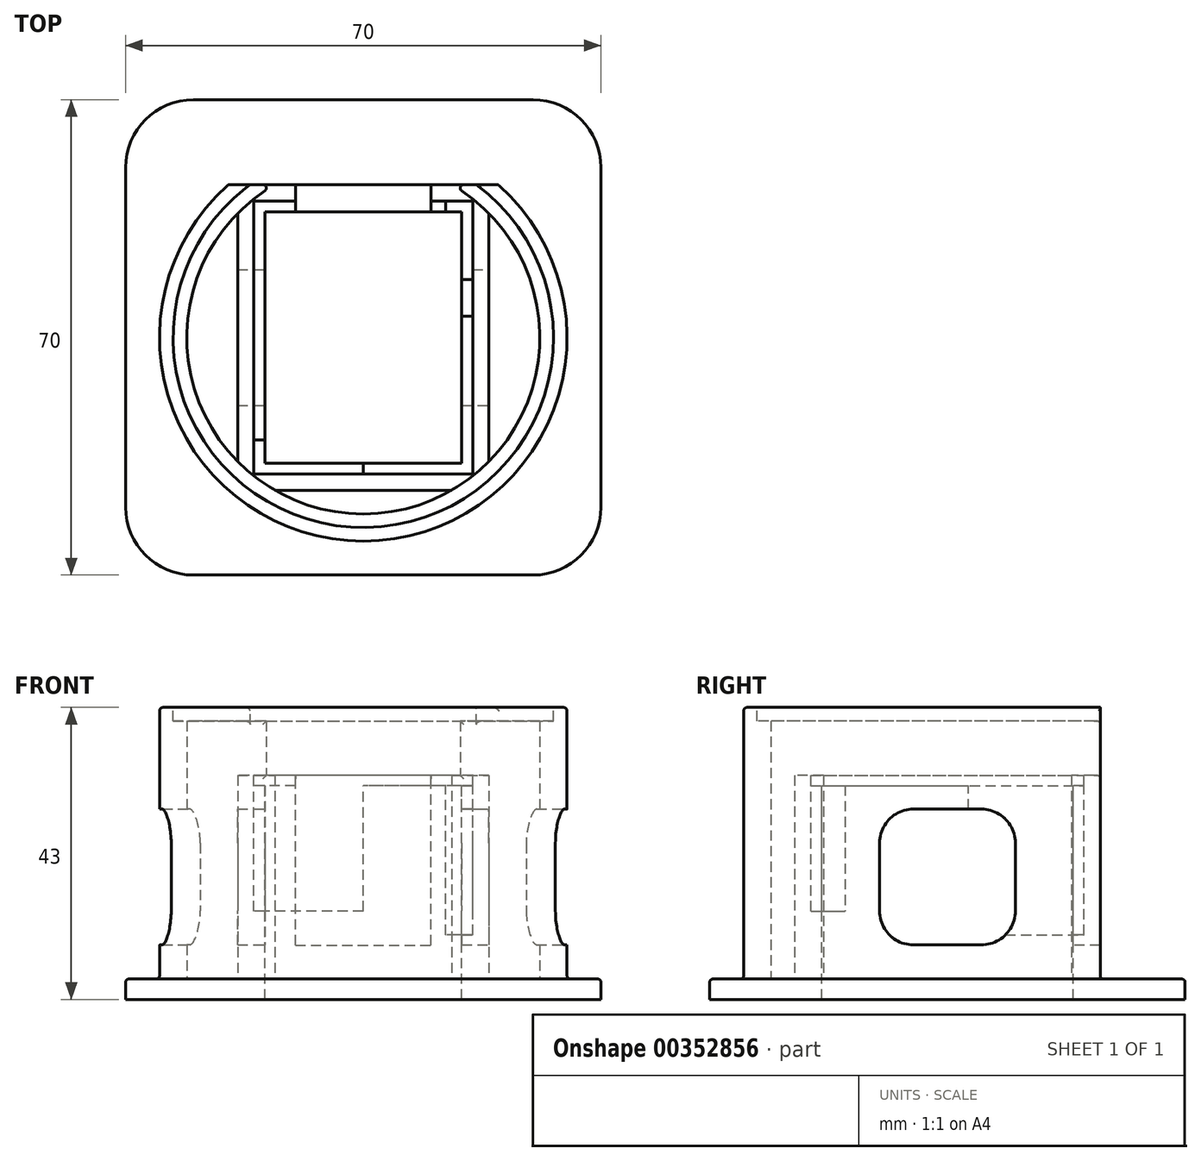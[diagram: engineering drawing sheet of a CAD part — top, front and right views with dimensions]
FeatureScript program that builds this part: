
annotation { "Feature Type Name" : "Feature", "Feature Type Description" : "" }
export const myFeature = defineFeature(function(context is Context, id is Id, definition is map)
    precondition{}
    {
        {
            var Q0;
            Q0=qCreatedBy(makeId("Top.planeOp"),FACE);
            var sketch = newSketch(context, id + "F0", { "sketchPlane" : qUnion([Q0])});
            skLineSegment(sketch, "E0.bottom", {"start": v(25, -35) * mm, "end": v(-25, -35) * mm});
            skLineSegment(sketch, "E0.top", {"start": v(25, 35) * mm, "end": v(-25, 35) * mm});
            skLineSegment(sketch, "E0.left", {"start": v(35, -25) * mm, "end": v(35, 25) * mm});
            skLineSegment(sketch, "E0.right", {"start": v(-35, -25) * mm, "end": v(-35, 25) * mm});
            skPoint(sketch, "E0.middle", {"position": v(0, 0) * mm});
            skPoint(sketch, "E1.visualSharp", {"position": v(-35, -35) * mm});
            skArc(sketch, "E1.filletArc", {"start": v(-35, -25) * mm, "mid": v(-32.07, -32.07) * mm, "end": v(-25, -35) * mm});
            skPoint(sketch, "E2.visualSharp", {"position": v(35, -35) * mm});
            skArc(sketch, "E2.filletArc", {"start": v(25, -35) * mm, "mid": v(32.07, -32.07) * mm, "end": v(35, -25) * mm});
            skPoint(sketch, "E3.visualSharp", {"position": v(35, 35) * mm});
            skArc(sketch, "E3.filletArc", {"start": v(35, 25) * mm, "mid": v(32.07, 32.07) * mm, "end": v(25, 35) * mm});
            skPoint(sketch, "E4.visualSharp", {"position": v(-35, 35) * mm});
            skArc(sketch, "E4.filletArc", {"start": v(-25, 35) * mm, "mid": v(-32.07, 32.07) * mm, "end": v(-35, 25) * mm});
            skSolve(sketch);
        }
        {
            var Q0;
            Q0 = qSketchRegion(id + "F0", true);
            extrude(context, id + "F1", {"entities" : qUnion([Q0]), "depth" : 3 * mm, "offsetDistance" : 25 * mm});
        }
        {
            var Q0;
            Q0=makeQuery(id+"F1.opExtrude","CAP_FACE",FACE,{"disambiguationData":[OSD([sQuery(id+"F0.wireOp",EDGE,"E0.bottom"),sQuery(id+"F0.wireOp",EDGE,"E0.top"),sQuery(id+"F0.wireOp",EDGE,"E0.left"),sQuery(id+"F0.wireOp",EDGE,"E0.right"),sQuery(id+"F0.wireOp",EDGE,"E1.filletArc"),sQuery(id+"F0.wireOp",EDGE,"E2.filletArc"),sQuery(id+"F0.wireOp",EDGE,"E3.filletArc"),sQuery(id+"F0.wireOp",EDGE,"E4.filletArc")])],"isStart":false});
            var sketch = newSketch(context, id + "F2", { "sketchPlane" : qUnion([Q0])});
            skLineSegment(sketch, "E5.bottom", {"start": v(16.5, -22.5) * mm, "end": v(-16.5, -22.5) * mm});
            skLineSegment(sketch, "E5.top", {"start": v(16.5, 22.5) * mm, "end": v(-16.5, 22.5) * mm});
            skLineSegment(sketch, "E5.left", {"start": v(18.5, -20.5) * mm, "end": v(18.5, 20.5) * mm});
            skLineSegment(sketch, "E5.right", {"start": v(-18.5, -20.5) * mm, "end": v(-18.5, 20.5) * mm});
            skPoint(sketch, "E5.middle", {"position": v(0, 0) * mm});
            skPoint(sketch, "E6.visualSharp", {"position": v(18.5, -22.5) * mm});
            skArc(sketch, "E6.filletArc", {"start": v(16.5, -22.5) * mm, "mid": v(17.91, -21.91) * mm, "end": v(18.5, -20.5) * mm});
            skPoint(sketch, "E7.visualSharp", {"position": v(18.5, 22.5) * mm});
            skArc(sketch, "E7.filletArc", {"start": v(18.5, 20.5) * mm, "mid": v(17.91, 21.91) * mm, "end": v(16.5, 22.5) * mm});
            skPoint(sketch, "E8.visualSharp", {"position": v(-18.5, 22.5) * mm});
            skArc(sketch, "E8.filletArc", {"start": v(-16.5, 22.5) * mm, "mid": v(-17.91, 21.91) * mm, "end": v(-18.5, 20.5) * mm});
            skPoint(sketch, "E9.visualSharp", {"position": v(-18.5, -22.5) * mm});
            skArc(sketch, "E9.filletArc", {"start": v(-18.5, -20.5) * mm, "mid": v(-17.91, -21.91) * mm, "end": v(-16.5, -22.5) * mm});
            skSolve(sketch);
        }
        {
            var Q0;
            Q0=makeQuery(id+"F2.imprint","IMPRINT",FACE,{"disambiguationData":[TD([[makeQuery(id+"F2.imprint","IMPRINT",EDGE,{"derivedFrom":sQuery(id+"F2.wireOp",EDGE,"E5.bottom")}),-1.0]])]});
            extrude(context, id + "F3", {"entities" : qUnion([Q0]), "operationType" : NewBodyOperationType.ADD, "depth" : 30 * mm, "offsetDistance" : 25 * mm});
        }
        {
            var Q0;
            Q0=makeQuery(id+"F3.opExtrude","CAP_FACE",FACE,{"disambiguationData":[OSD([sQuery(id+"F2.wireOp",EDGE,"E5.bottom"),sQuery(id+"F2.wireOp",EDGE,"E5.top"),sQuery(id+"F2.wireOp",EDGE,"E5.left"),sQuery(id+"F2.wireOp",EDGE,"E5.right"),sQuery(id+"F2.wireOp",EDGE,"E6.filletArc"),sQuery(id+"F2.wireOp",EDGE,"E7.filletArc"),sQuery(id+"F2.wireOp",EDGE,"E8.filletArc"),sQuery(id+"F2.wireOp",EDGE,"E9.filletArc")])],"isStart":false});
            var sketch = newSketch(context, id + "F4", { "sketchPlane" : qUnion([Q0])});
            skLineSegment(sketch, "E10.bottom", {"start": v(-14.5, 18.5) * mm, "end": v(14.5, 18.5) * mm});
            skLineSegment(sketch, "E10.top", {"start": v(-14.5, -18.5) * mm, "end": v(14.5, -18.5) * mm});
            skLineSegment(sketch, "E10.left", {"start": v(-14.5, 18.5) * mm, "end": v(-14.5, -18.5) * mm});
            skLineSegment(sketch, "E10.right", {"start": v(14.5, 18.5) * mm, "end": v(14.5, -18.5) * mm});
            skPoint(sketch, "E10.middle", {"position": v(0, 0) * mm});
            skSolve(sketch);
        }
        {
            var Q0;
            Q0=makeQuery(id+"F4.imprint","IMPRINT",FACE,{"disambiguationData":[TD([[makeQuery(id+"F4.imprint","IMPRINT",EDGE,{"derivedFrom":sQuery(id+"F4.wireOp",EDGE,"E10.bottom")}),-1.0]])]});
            extrude(context, id + "F5", {"entities" : qUnion([Q0]), "operationType" : NewBodyOperationType.REMOVE, "endBound" : BoundingType.THROUGH_ALL, "oppositeDirection" : true, "depth" : 25 * mm});
        }
        {
            var Q0;
            Q0=makeQuery(id+"F3.opExtrude","CAP_FACE",FACE,{"disambiguationData":[OSD([sQuery(id+"F2.wireOp",EDGE,"E5.bottom"),sQuery(id+"F2.wireOp",EDGE,"E5.top"),sQuery(id+"F2.wireOp",EDGE,"E5.left"),sQuery(id+"F2.wireOp",EDGE,"E5.right"),sQuery(id+"F2.wireOp",EDGE,"E6.filletArc"),sQuery(id+"F2.wireOp",EDGE,"E7.filletArc"),sQuery(id+"F2.wireOp",EDGE,"E8.filletArc"),sQuery(id+"F2.wireOp",EDGE,"E9.filletArc")])],"isStart":false});
            var sketch = newSketch(context, id + "F6", { "sketchPlane" : qUnion([Q0])});
            skLineSegment(sketch, "E11.bottom", {"start": v(16.1, -20.1) * mm, "end": v(-16.1, -20.1) * mm});
            skLineSegment(sketch, "E11.top", {"start": v(16.1, 20.1) * mm, "end": v(-16.1, 20.1) * mm});
            skLineSegment(sketch, "E11.left", {"start": v(16.1, -20.1) * mm, "end": v(16.1, 20.1) * mm});
            skLineSegment(sketch, "E11.right", {"start": v(-16.1, -20.1) * mm, "end": v(-16.1, 20.1) * mm});
            skPoint(sketch, "E11.middle", {"position": v(0, 0) * mm});
            skSolve(sketch);
        }
        {
            var Q0;
            Q0 = qSketchRegion(id + "F6", true);
            extrude(context, id + "F7", {"entities" : qUnion([Q0]), "operationType" : NewBodyOperationType.REMOVE, "oppositeDirection" : true, "depth" : 1.5 * mm});
        }
        {
            var Q0;
            Q0=makeQuery(id+"F7.boolean.opBoolean","COPY",FACE,{"derivedFrom":makeQuery(id+"F7.opExtrude","CAP_FACE",FACE,{"disambiguationData":[OSD([sQuery(id+"F6.wireOp",EDGE,"E11.bottom"),sQuery(id+"F6.wireOp",EDGE,"E11.top"),sQuery(id+"F6.wireOp",EDGE,"E11.left"),sQuery(id+"F6.wireOp",EDGE,"E11.right")])],"isStart":false})});
            var sketch = newSketch(context, id + "F8", { "sketchPlane" : qUnion([Q0])});
            skLineSegment(sketch, "E12.bottom", {"start": v(12.1, 20.1) * mm, "end": v(16.1, 20.1) * mm});
            skLineSegment(sketch, "E12.top", {"start": v(12.1, 3.1) * mm, "end": v(16.1, 3.1) * mm});
            skLineSegment(sketch, "E12.left", {"start": v(12.1, 20.1) * mm, "end": v(12.1, 3.1) * mm});
            skLineSegment(sketch, "E12.right", {"start": v(16.1, 20.1) * mm, "end": v(16.1, 3.1) * mm});
            skSolve(sketch);
        }
        {
            var Q0;
            {var subQ0=sQuery(id+"F8.wireOp",EDGE,"E12.right");var subQ1=sQuery(id+"F8.wireOp",EDGE,"E12.top");var subQ2=makeQuery(id+"F8.imprint","INTERSECT",VERTEX,{"derivedFrom":[subQ1,subQ0]});Q0=makeQuery(id+"F8.imprint","IMPRINT",FACE,{"disambiguationData":[TD([[makeQuery(id+"F8.imprint","IMPRINT",EDGE,{"disambiguationData":[TD([[subQ2,1.0]])],"derivedFrom":subQ1}),1.0]])]});}
            var Q1;
            {var subQ1=sQuery(id+"F8.wireOp",EDGE,"E12.bottom");Q1=makeQuery(id+"F8.imprint","IMPRINT",FACE,{"disambiguationData":[TD([[makeQuery(id+"F8.imprint","IMPRINT",EDGE,{"derivedFrom":subQ1}),1.0]])]});}
            extrude(context, id + "F9", {"entities" : qUnion([Q0, Q1]), "operationType" : NewBodyOperationType.REMOVE, "oppositeDirection" : true, "depth" : 22 * mm});
        }
        {
            var Q0;
            Q0=makeQuery(id+"F3.opExtrude","CAP_FACE",FACE,{"disambiguationData":[OSD([sQuery(id+"F2.wireOp",EDGE,"E5.bottom"),sQuery(id+"F2.wireOp",EDGE,"E5.top"),sQuery(id+"F2.wireOp",EDGE,"E5.left"),sQuery(id+"F2.wireOp",EDGE,"E5.right"),sQuery(id+"F2.wireOp",EDGE,"E6.filletArc"),sQuery(id+"F2.wireOp",EDGE,"E7.filletArc"),sQuery(id+"F2.wireOp",EDGE,"E8.filletArc"),sQuery(id+"F2.wireOp",EDGE,"E9.filletArc")])],"isStart":false});
            var sketch = newSketch(context, id + "F10", { "sketchPlane" : qUnion([Q0])});
            skLineSegment(sketch, "E13.bottom", {"start": v(-10, 22.5) * mm, "end": v(10, 22.5) * mm});
            skLineSegment(sketch, "E13.top", {"start": v(-10, 18.5) * mm, "end": v(10, 18.5) * mm});
            skLineSegment(sketch, "E13.left", {"start": v(-10, 22.5) * mm, "end": v(-10, 18.5) * mm});
            skLineSegment(sketch, "E13.right", {"start": v(10, 22.5) * mm, "end": v(10, 18.5) * mm});
            skSolve(sketch);
        }
        {
            var Q0;
            Q0 = qSketchRegion(id + "F10", true);
            extrude(context, id + "F11", {"entities" : qUnion([Q0]), "operationType" : NewBodyOperationType.REMOVE, "oppositeDirection" : true, "depth" : 25 * mm, "offsetDistance" : 25 * mm});
        }
        {
            var Q0;
            Q0=makeQuery(id+"F3.opExtrude","CAP_FACE",FACE,{"disambiguationData":[OSD([sQuery(id+"F2.wireOp",EDGE,"E5.bottom"),sQuery(id+"F2.wireOp",EDGE,"E5.top"),sQuery(id+"F2.wireOp",EDGE,"E5.left"),sQuery(id+"F2.wireOp",EDGE,"E5.right"),sQuery(id+"F2.wireOp",EDGE,"E6.filletArc"),sQuery(id+"F2.wireOp",EDGE,"E7.filletArc"),sQuery(id+"F2.wireOp",EDGE,"E8.filletArc"),sQuery(id+"F2.wireOp",EDGE,"E9.filletArc")])],"isStart":false});
            var sketch = newSketch(context, id + "F12", { "sketchPlane" : qUnion([Q0])});
            skLineSegment(sketch, "E14.bottom", {"start": v(0, -20.1) * mm, "end": v(-16.1, -20.1) * mm});
            skLineSegment(sketch, "E14.top", {"start": v(0, -15.1) * mm, "end": v(-16.1, -15.1) * mm});
            skLineSegment(sketch, "E14.left", {"start": v(0, -20.1) * mm, "end": v(0, -15.1) * mm});
            skLineSegment(sketch, "E14.right", {"start": v(-16.1, -20.1) * mm, "end": v(-16.1, -15.1) * mm});
            skSolve(sketch);
        }
        {
            var Q0;
            Q0 = qSketchRegion(id + "F12", true);
            extrude(context, id + "F13", {"entities" : qUnion([Q0]), "operationType" : NewBodyOperationType.REMOVE, "oppositeDirection" : true, "depth" : 20 * mm, "offsetDistance" : 25 * mm});
        }
        {
            var Q0;
            Q0=makeQuery(id+"F1.opExtrude","CAP_FACE",FACE,{"disambiguationData":[OSD([sQuery(id+"F0.wireOp",EDGE,"E0.bottom"),sQuery(id+"F0.wireOp",EDGE,"E0.top"),sQuery(id+"F0.wireOp",EDGE,"E0.left"),sQuery(id+"F0.wireOp",EDGE,"E0.right"),sQuery(id+"F0.wireOp",EDGE,"E1.filletArc"),sQuery(id+"F0.wireOp",EDGE,"E2.filletArc"),sQuery(id+"F0.wireOp",EDGE,"E3.filletArc"),sQuery(id+"F0.wireOp",EDGE,"E4.filletArc")])],"isStart":false});
            var sketch = newSketch(context, id + "F14", { "sketchPlane" : qUnion([Q0])});
            skArc(sketch, "E15", {"start": v(-19.84, 22.5) * mm, "mid": v(0, -30) * mm, "end": v(19.84, 22.5) * mm});
            skArc(sketch, "E16.0", {"start": v(-13.03, 22.5) * mm, "mid": v(0, -26) * mm, "end": v(13.03, 22.5) * mm});
            skLineSegment(sketch, "E17", {"start": v(13.03, 22.5) * mm, "end": v(19.84, 22.5) * mm});
            skLineSegment(sketch, "E18", {"start": v(19.84, 22.5) * mm, "end": v(13.03, 22.5) * mm});
            skLineSegment(sketch, "E19.trimOffspring", {"start": v(-13.03, 22.5) * mm, "end": v(-19.84, 22.5) * mm});
            skSolve(sketch);
        }
        {
            var Q0;
            Q0 = qSketchRegion(id + "F14", true);
            extrude(context, id + "F15", {"entities" : qUnion([Q0]), "operationType" : NewBodyOperationType.ADD, "depth" : 40 * mm, "offsetDistance" : 25 * mm});
        }
        {
            var Q0;
            Q0=makeQuery(id+"F15.opExtrude","CAP_FACE",FACE,{"disambiguationData":[OSD([sQuery(id+"F14.wireOp",EDGE,"E15"),sQuery(id+"F14.wireOp",EDGE,"E16.0"),sQuery(id+"F14.wireOp",EDGE,"E18"),sQuery(id+"F14.wireOp",EDGE,"E19.trimOffspring")])],"isStart":false});
            var sketch = newSketch(context, id + "F16", { "sketchPlane" : qUnion([Q0])});
            skCircle(sketch, "E20", {"center": v(0, 0) * mm, "radius": 28 * mm});
            skSolve(sketch);
        }
        {
            var Q0;
            Q0 = qSketchRegion(id + "F16", true);
            extrude(context, id + "F17", {"entities" : qUnion([Q0]), "operationType" : NewBodyOperationType.REMOVE, "oppositeDirection" : true, "depth" : 2 * mm, "offsetDistance" : 25 * mm});
        }
        {
            var Q0;
            Q0=makeQuery(id+"F7.boolean.opBoolean","COPY",EDGE,{"derivedFrom":makeQuery(id+"F7.opExtrude","CAP_EDGE",EDGE,{"disambiguationData":[OSD([sQuery(id+"F6.wireOp",EDGE,"E11.right")])],"isStart":true})});
            var Q1;
            {var subQ0=sQuery(id+"F6.wireOp",EDGE,"E11.top");Q1=makeQuery(id+"F11.boolean.opBoolean","SPLIT",EDGE,{"disambiguationData":[TD([makeQuery(id+"F7.boolean.opBoolean","COPY",FACE,{"derivedFrom":makeQuery(id+"F7.opExtrude","SWEPT_FACE",FACE,{"disambiguationData":[OSD([sQuery(id+"F6.wireOp",EDGE,"E11.left")])]})})])],"derivedFrom":makeQuery(id+"F7.boolean.opBoolean","COPY",EDGE,{"derivedFrom":makeQuery(id+"F7.opExtrude","CAP_EDGE",EDGE,{"disambiguationData":[OSD([subQ0])],"isStart":true})})});}
            var Q2;
            Q2=makeQuery(id+"F7.boolean.opBoolean","COPY",EDGE,{"derivedFrom":makeQuery(id+"F7.opExtrude","CAP_EDGE",EDGE,{"disambiguationData":[OSD([sQuery(id+"F6.wireOp",EDGE,"E11.left")])],"isStart":true})});
            var Q3;
            Q3=makeQuery(id+"F7.boolean.opBoolean","COPY",EDGE,{"derivedFrom":makeQuery(id+"F7.opExtrude","CAP_EDGE",EDGE,{"disambiguationData":[OSD([sQuery(id+"F6.wireOp",EDGE,"E11.bottom")])],"isStart":true})});
            var Q4;
            Q4=makeQuery(id+"F17.boolean.opBoolean","COPY",EDGE,{"derivedFrom":makeQuery(id+"F17.opExtrude","CAP_EDGE",EDGE,{"disambiguationData":[OSD([sQuery(id+"F16.wireOp",EDGE,"E20")])],"isStart":true})});
            var Q5;
            Q5=makeQuery(id+"F15.opExtrude","CAP_EDGE",EDGE,{"disambiguationData":[OSD([sQuery(id+"F14.wireOp",EDGE,"E19.trimOffspring")])],"isStart":false});
            var Q6;
            Q6=makeQuery(id+"F17.boolean.opBoolean","INTERSECT",EDGE,{"disambiguationData":[OD(0.0)],"derivedFrom":[makeQuery(id+"F15.boolean.opBoolean","MERGE",FACE,{"derivedFrom":[makeQuery(id+"F3.opExtrude","SWEPT_FACE",FACE,{"disambiguationData":[OSD([sQuery(id+"F2.wireOp",EDGE,"E5.top")])]}),makeQuery(id+"F15.opExtrude","SWEPT_FACE",FACE,{"disambiguationData":[OSD([sQuery(id+"F14.wireOp",EDGE,"E18")])]}),makeQuery(id+"F15.opExtrude","SWEPT_FACE",FACE,{"disambiguationData":[OSD([sQuery(id+"F14.wireOp",EDGE,"E19.trimOffspring")])]})]}),makeQuery(id+"F17.opExtrude","CAP_FACE",FACE,{"disambiguationData":[OSD([sQuery(id+"F16.wireOp",EDGE,"E20")])],"isStart":false})]});
            var Q7;
            {var subQ0=sQuery(id+"F2.wireOp",EDGE,"E7.filletArc");var subQ1=sQuery(id+"F2.wireOp",EDGE,"E5.top");Q7=makeQuery(id+"F11.boolean.opBoolean","SPLIT",EDGE,{"disambiguationData":[TD([makeQuery(id+"F3.opExtrude","SWEPT_FACE",FACE,{"disambiguationData":[OSD([subQ0])]})])],"derivedFrom":makeQuery(id+"F3.opExtrude","CAP_EDGE",EDGE,{"disambiguationData":[OSD([subQ1])],"isStart":false})});}
            var Q8;
            Q8=makeQuery(id+"F17.boolean.opBoolean","INTERSECT",EDGE,{"disambiguationData":[OD(1.0)],"derivedFrom":[makeQuery(id+"F15.boolean.opBoolean","MERGE",FACE,{"derivedFrom":[makeQuery(id+"F3.opExtrude","SWEPT_FACE",FACE,{"disambiguationData":[OSD([sQuery(id+"F2.wireOp",EDGE,"E5.top")])]}),makeQuery(id+"F15.opExtrude","SWEPT_FACE",FACE,{"disambiguationData":[OSD([sQuery(id+"F14.wireOp",EDGE,"E18")])]}),makeQuery(id+"F15.opExtrude","SWEPT_FACE",FACE,{"disambiguationData":[OSD([sQuery(id+"F14.wireOp",EDGE,"E19.trimOffspring")])]})]}),makeQuery(id+"F17.opExtrude","CAP_FACE",FACE,{"disambiguationData":[OSD([sQuery(id+"F16.wireOp",EDGE,"E20")])],"isStart":false})]});
            var Q9;
            Q9=makeQuery(id+"F15.opExtrude","CAP_EDGE",EDGE,{"disambiguationData":[OSD([sQuery(id+"F14.wireOp",EDGE,"E15")])],"isStart":false});
            var Q10;
            {var subQ0=sQuery(id+"F2.wireOp",EDGE,"E8.filletArc");var subQ1=sQuery(id+"F2.wireOp",EDGE,"E5.top");Q10=makeQuery(id+"F11.boolean.opBoolean","SPLIT",EDGE,{"disambiguationData":[TD([makeQuery(id+"F3.opExtrude","SWEPT_FACE",FACE,{"disambiguationData":[OSD([subQ0])]})])],"derivedFrom":makeQuery(id+"F3.opExtrude","CAP_EDGE",EDGE,{"disambiguationData":[OSD([subQ1])],"isStart":false})});}
            var Q11;
            Q11=makeQuery(id+"F15.opExtrude","SWEPT_EDGE",EDGE,{"disambiguationData":[OSD([sQuery(id+"F2.wireOp",EDGE,"E5.top"),sQuery(id+"F14.wireOp",EDGE,"E16.0"),sQuery(id+"F14.wireOp",EDGE,"E19.trimOffspring")])]});
            var Q12;
            Q12=makeQuery(id+"F15.opExtrude","SWEPT_EDGE",EDGE,{"disambiguationData":[OSD([sQuery(id+"F2.wireOp",EDGE,"E5.top"),sQuery(id+"F14.wireOp",EDGE,"E16.0"),sQuery(id+"F14.wireOp",EDGE,"E18")])]});
            var Q13;
            Q13=makeQuery(id+"F15.opExtrude","SWEPT_EDGE",EDGE,{"disambiguationData":[OSD([sQuery(id+"F14.wireOp",EDGE,"E15"),sQuery(id+"F14.wireOp",EDGE,"E19.trimOffspring")])]});
            var Q14;
            Q14=makeQuery(id+"F15.opExtrude","SWEPT_EDGE",EDGE,{"disambiguationData":[OSD([sQuery(id+"F14.wireOp",EDGE,"E15"),sQuery(id+"F14.wireOp",EDGE,"E18")])]});
            var Q15;
            Q15=makeQuery(id+"F11.boolean.opBoolean","COPY",EDGE,{"derivedFrom":makeQuery(id+"F11.opExtrude","SWEPT_EDGE",EDGE,{"disambiguationData":[OSD([sQuery(id+"F2.wireOp",EDGE,"E5.top"),sQuery(id+"F10.wireOp",EDGE,"E13.bottom"),sQuery(id+"F10.wireOp",EDGE,"E13.right")])]})});
            var Q16;
            Q16=makeQuery(id+"F11.boolean.opBoolean","COPY",EDGE,{"derivedFrom":makeQuery(id+"F11.opExtrude","CAP_EDGE",EDGE,{"disambiguationData":[OSD([sQuery(id+"F10.wireOp",EDGE,"E13.bottom")])],"isStart":false})});
            var Q17;
            Q17=makeQuery(id+"F11.boolean.opBoolean","COPY",EDGE,{"derivedFrom":makeQuery(id+"F11.opExtrude","SWEPT_EDGE",EDGE,{"disambiguationData":[OSD([sQuery(id+"F2.wireOp",EDGE,"E5.top"),sQuery(id+"F10.wireOp",EDGE,"E13.bottom"),sQuery(id+"F10.wireOp",EDGE,"E13.left")])]})});
            var Q18;
            {var subQ0=sQuery(id+"F0.wireOp",EDGE,"E4.filletArc");var subQ1=sQuery(id+"F0.wireOp",EDGE,"E3.filletArc");var subQ2=sQuery(id+"F0.wireOp",EDGE,"E2.filletArc");var subQ3=sQuery(id+"F0.wireOp",EDGE,"E1.filletArc");var subQ4=sQuery(id+"F0.wireOp",EDGE,"E0.bottom");var subQ5=sQuery(id+"F0.wireOp",EDGE,"E0.right");var subQ6=sQuery(id+"F0.wireOp",EDGE,"E0.top");var subQ7=sQuery(id+"F0.wireOp",EDGE,"E0.left");Q18=makeQuery(id+"F15.boolean.opBoolean","SPLIT",FACE,{"disambiguationData":[TD([makeQuery(id+"F1.opExtrude","SWEPT_FACE",FACE,{"disambiguationData":[OSD([subQ4])]})])],"derivedFrom":makeQuery(id+"F1.opExtrude","CAP_FACE",FACE,{"disambiguationData":[OSD([subQ4,subQ6,subQ7,subQ5,subQ3,subQ2,subQ1,subQ0])],"isStart":false})});}
            fillet(context, id + "F18", {"entities" : qUnion([Q0, Q1, Q2, Q3, Q4, Q5, Q6, Q7, Q8, Q9, Q10, Q11, Q12, Q13, Q14, Q15, Q16, Q17, Q18]), "radius" : 0.5 * mm, "tangentPropagation" : true, "allowEdgeOverflow" : false});
        }
        {
            var Q0;
            Q0=makeQuery(id+"F3.opExtrude","SWEPT_FACE",FACE,{"disambiguationData":[OSD([sQuery(id+"F2.wireOp",EDGE,"E5.left")])]});
            var sketch = newSketch(context, id + "F19", { "sketchPlane" : qUnion([Q0])});
            skLineSegment(sketch, "E21.bottom", {"start": v(5, 8.03) * mm, "end": v(-5, 8.03) * mm});
            skLineSegment(sketch, "E21.top", {"start": v(5, 28.03) * mm, "end": v(-5, 28.03) * mm});
            skLineSegment(sketch, "E21.left", {"start": v(10, 13.03) * mm, "end": v(10, 23.03) * mm});
            skLineSegment(sketch, "E21.right", {"start": v(-10, 13.03) * mm, "end": v(-10, 23.03) * mm});
            skPoint(sketch, "E21.middle", {"position": v(0, 18.03) * mm});
            skPoint(sketch, "E22.visualSharp", {"position": v(10, 8.03) * mm});
            skArc(sketch, "E22.filletArc", {"start": v(5, 8.03) * mm, "mid": v(8.54, 9.5) * mm, "end": v(10, 13.03) * mm});
            skPoint(sketch, "E23.visualSharp", {"position": v(-10, 8.03) * mm});
            skArc(sketch, "E23.filletArc", {"start": v(-10, 13.03) * mm, "mid": v(-8.54, 9.5) * mm, "end": v(-5, 8.03) * mm});
            skPoint(sketch, "E24.visualSharp", {"position": v(-10, 28.03) * mm});
            skArc(sketch, "E24.filletArc", {"start": v(-5, 28.03) * mm, "mid": v(-8.54, 26.57) * mm, "end": v(-10, 23.03) * mm});
            skPoint(sketch, "E25.visualSharp", {"position": v(10, 28.03) * mm});
            skArc(sketch, "E25.filletArc", {"start": v(10, 23.03) * mm, "mid": v(8.54, 26.57) * mm, "end": v(5, 28.03) * mm});
            skSolve(sketch);
        }
        {
            var Q0;
            Q0 = qSketchRegion(id + "F19", true);
            extrude(context, id + "F20", {"entities" : qUnion([Q0]), "operationType" : NewBodyOperationType.REMOVE, "endBound" : BoundingType.THROUGH_ALL, "oppositeDirection" : true, "depth" : 25 * mm, "offsetDistance" : 25 * mm, "hasSecondDirection" : true, "secondDirectionBound" : SecondDirectionBoundingType.THROUGH_ALL, "secondDirectionOppositeDirection" : false, "secondDirectionDepth" : 25 * mm});
        }
    });
